# Revit family: 17.  Канальный осевой вентилятор FE Тип A
name_source: partatom
category: Оборудование
revit_build: Autodesk Revit 2016 (Build: 20151209_0715(x64)
units: mm (PartAtom-declared; Revit-internal decimal feet)

## family parameters
Всегда вертикально = Да
На основе рабочей плоскости = Нет
Общий = Нет
При загрузке вырезать с полостями = Нет
Размер круглого соединителя = Использовать диаметр
Тип детали = Нормальный
Точка расчета площади = Нет

## types (13) — shared parameters
R скругления = 15 мм
Единица измерения = шт.
Завод изготовитель = KORF
И = 72 мм
И1 = 43 мм
И2 = 65 мм
Ключевая пометка = Вентиляция
Материал = Сталь серая
Наименование и тех.хар-ка = Канальный осевой вентилятор
Раздел = ОВ
отступ = 32 мм

## per-type parameters (varying)
| type | D | D1 | D2 | d | d1 | d2 | А | А1 | Б | Г | Д | Д1 | Д2 | Е | Ж | Масса единицы | Мощность, кВт | Размер В | Сила тока J, А | Тип, марка, обозначение | Частота вращения n, об/мин |
| FE031-4DF | 158 мм | 191 мм | 115 мм | 76 мм | 191 мм | 115 мм | 356 мм | 178 мм | 8 мм | 382 мм | 317 мм | 307 мм | 158 мм | 17 мм | 135 мм | 6.5 кг | 0 Вт | 10 мм | 0.29 | FE031-4DF.OC.V7 | 1410 |
| FE031-4EF | 158 мм | 191 мм | 115 мм | 76 мм | 191 мм | 115 мм | 356 мм | 178 мм | 8 мм | 382 мм | 317 мм | 307 мм | 158 мм | 17 мм | 135 мм | 6.5 кг | 0 Вт | 10 мм | 0.59 | FE031-4EF.OC.V7 | 1400 |
| FE035-4DF | 178 мм | 211 мм | 126 мм | 84 мм | 211 мм | 126 мм | 395 мм | 198 мм | 8 мм | 421 мм | 356 мм | 346 мм | 178 мм | 17 мм | 135 мм | 7.2 кг | 0 Вт | 10 мм | 0.35 | FE035-4DF.OC.V7 | 1360 |
| FE035-4EF | 178 мм | 211 мм | 126 мм | 84 мм | 211 мм | 126 мм | 395 мм | 198 мм | 8 мм | 421 мм | 356 мм | 346 мм | 178 мм | 17 мм | 135 мм | 7.5 кг | 0 Вт | 10 мм | 0.9 | FE035-4EF.OF.V7 | 1400 |
| FE040-VDF | 200 мм | 233 мм | 140 мм | 93 мм | 233 мм | 140 мм | 438 мм | 219 мм | 12 мм | 466 мм | 400 мм | 390 мм | 200 мм | 18 мм | 155 мм | 8.6 кг | 0 Вт | 10 мм | 0.48 | FE040-VDF.2C.V7 | 1300 |
| FE040-4EF | 200 мм | 233 мм | 140 мм | 93 мм | 233 мм | 140 мм | 438 мм | 219 мм | 12 мм | 466 мм | 400 мм | 390 мм | 200 мм | 18 мм | 155 мм | 10.3 кг | 0 Вт | 10 мм | 1.35 | FE040-4EF.2F.V7 | 1320 |
| FE045-VDF | 226 мм | 258 мм | 155 мм | 103 мм | 258 мм | 155 мм | 487 мм | 244 мм | 12 мм | 515 мм | 451 мм | 441 мм | 226 мм | 22 мм | 160 мм | 14 кг | 1 Вт | 10 мм | 1.15 | FE045-VDF.4F.V7 | 1340 |
| FE050-SDF | 252 мм | 284 мм | 170 мм | 113 мм | 284 мм | 170 мм | 541 мм | 271 мм | 12 мм | 567 мм | 503 мм | 493 мм | 252 мм | 22 мм | 165 мм | 14.4 кг | 0 Вт | 10 мм | 0.74 | FE050-SDF.4F.V7 | 900 |
| FE050-6EF | 252 мм | 284 мм | 170 мм | 113 мм | 284 мм | 170 мм | 541 мм | 271 мм | 12 мм | 567 мм | 503 мм | 493 мм | 252 мм | 22 мм | 165 мм | 14.4 кг | 0 Вт | 10 мм | 1.25 | FE050-6EF.4F.V7 | 890 |
| FE056-SDF | 280 мм | 318 мм | 191 мм | 127 мм | 318 мм | 191 мм | 605 мм | 303 мм | 12 мм | 635 мм | 559 мм | 549 мм | 280 мм | 22 мм | 210 мм | 17 кг | 0 Вт | 12 мм | 0.76 | FE056-SDF.4F.V7 | 880 |
| FE056-6EF | 280 мм | 318 мм | 191 мм | 127 мм | 318 мм | 191 мм | 605 мм | 303 мм | 12 мм | 635 мм | 559 мм | 549 мм | 280 мм | 24 мм | 210 мм | 19 кг | 1 Вт | 12 мм | 2.3 | FE056-6EF.4F.V7 | 920 |
| FE063-VDF | 317 мм | 354 мм | 212 мм | 141 мм | 354 мм | 212 мм | 674 мм | 337 мм | 12 мм | 707 мм | 634 мм | 624 мм | 317 мм | 22 мм | 220 мм | 45 кг | 3 Вт | 12 мм | 4.8 | FE063-VDF.6N.V7 | 1310 |
| FE063-SDF | 317 мм | 354 мм | 212 мм | 141 мм | 354 мм | 212 мм | 674 мм | 337 мм | 12 мм | 707 мм | 634 мм | 624 мм | 317 мм | 22 мм | 220 мм | 21 кг | 1 Вт | 12 мм | 1.25 | FE063-SDF.6N.V7 | 900 |
